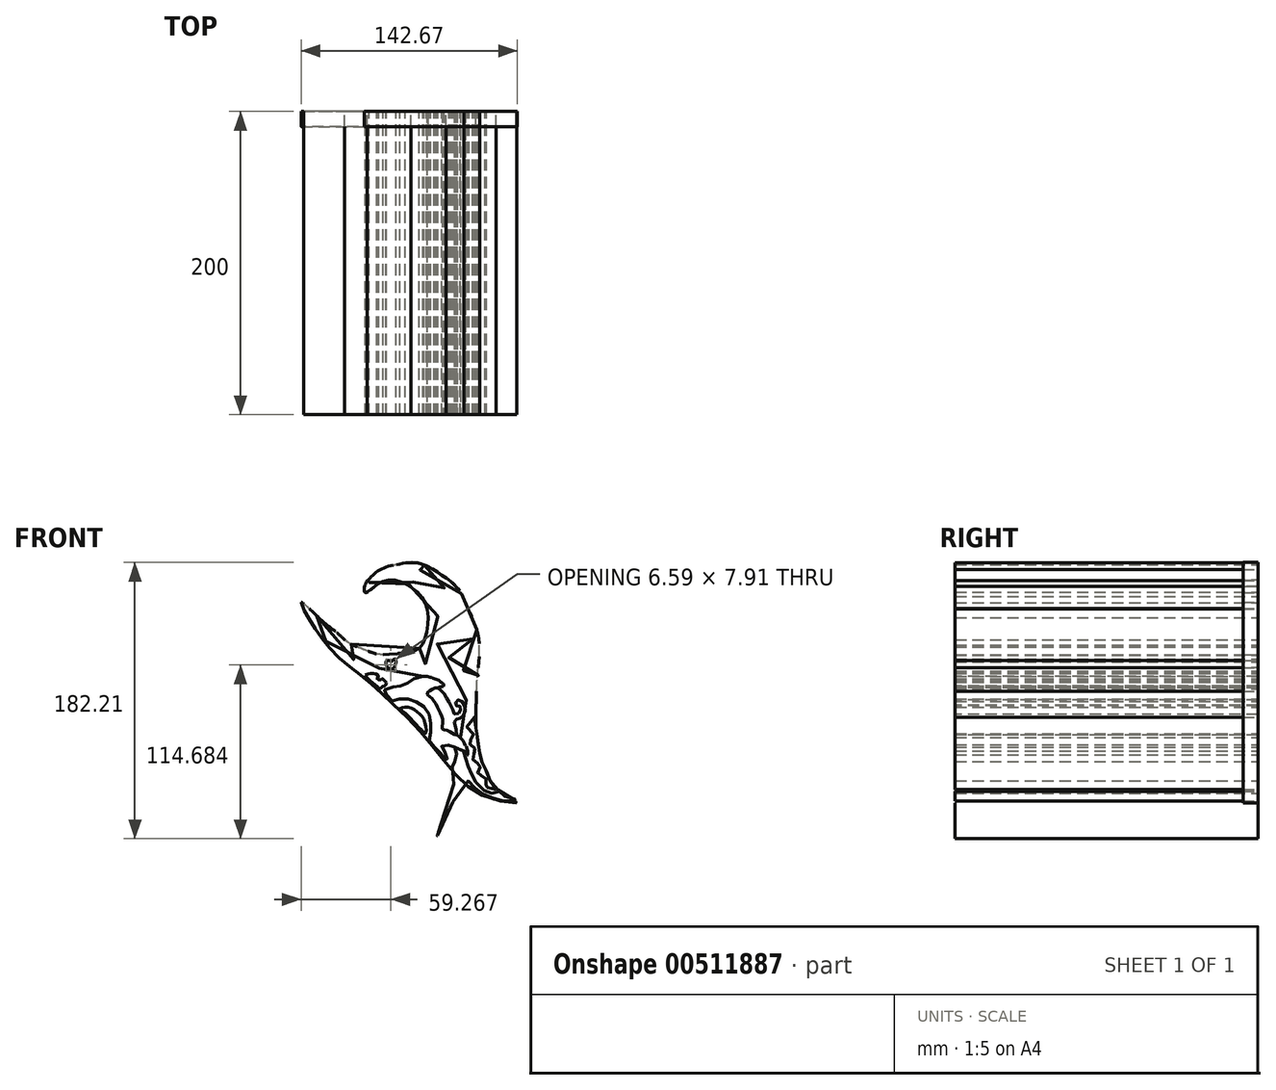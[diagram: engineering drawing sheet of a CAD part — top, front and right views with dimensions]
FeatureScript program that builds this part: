
annotation { "Feature Type Name" : "Feature", "Feature Type Description" : "" }
export const myFeature = defineFeature(function(context is Context, id is Id, definition is map)
    precondition{}
    {
        {
            var Q0;
            Q0=qCreatedBy(makeId("Front.planeOp"),FACE);
            var sketch = newSketch(context, id + "F0", { "sketchPlane" : qUnion([Q0])});
            skFitSpline(sketch, "E0", {"points": [v(-61.66, -100.95) * mm, v(-60.75, -105.22) * mm, v(-59.1, -108.17) * mm, v(-57.14, -111.12) * mm, v(-54.68, -114.57) * mm, v(-53.37, -117.36) * mm, v(-51.24, -119.98) * mm, v(-48.78, -124.4) * mm, v(-45.82, -127.69) * mm, v(-42.7, -130.8) * mm, v(-40.18, -133.76) * mm, v(-37.62, -136.55) * mm, v(-34.34, -139.83) * mm, v(-29.91, -143.1) * mm, v(-24.17, -146.39) * mm, v(-20.71, -144.2) * mm, v(-17.3, -143.74) * mm, v(-13.44, -143.59) * mm, v(-10.03, -145.44) * mm, v(-6.47, -148.54) * mm, v(-5.39, -151.48) * mm, v(-3.06, -153.34) * mm, v(-2.13, -150.7) * mm, v(0, -148.85) * mm, v(2.2, -147) * mm, v(4.83, -146.22) * mm, v(8.08, -146.06) * mm, v(11.64, -147) * mm, v(15.2, -148.08) * mm, v(16.9, -149.62) * mm, v(12.88, -150.4) * mm, v(9.48, -151.95) * mm, v(7.15, -153.5) * mm, v(4.52, -155.5) * mm, v(1.74, -155.82) * mm, v(0, -155.82) * mm, v(-3.53, -156.6) * mm, v(-7.09, -157.98) * mm, v(-9.41, -159.38) * mm, v(-7.45, -161.38) * mm, v(-4.91, -163.81) * mm, v(-2.96, -166.06) * mm, v(0, -164.89) * mm, v(2.8, -164.5) * mm, v(6.6, -164.5) * mm, v(10.6, -165.28) * mm, v(14, -167.03) * mm, v(17.42, -169.37) * mm, v(19.96, -172.5) * mm, v(21.61, -176.69) * mm, v(22.1, -180.5) * mm, v(22.2, -184.26) * mm, v(21.9, -188.03) * mm, v(20.92, -191.22) * mm, v(22.9, -193.83) * mm, v(25.33, -196.79) * mm, v(27.76, -199.17) * mm, v(29.97, -202.23) * mm, v(31.62, -204.43) * mm, v(33.96, -205.68) * mm, v(32.65, -203.33) * mm, v(31.69, -200.57) * mm, v(30.8, -198.23) * mm, v(30.03, -196.78) * mm, v(29.34, -195.6) * mm, v(31.69, -194.78) * mm, v(33.96, -194.85) * mm, v(35.83, -195.12) * mm, v(37.83, -196.02) * mm, v(39.27, -197.6) * mm, v(39.2, -200.85) * mm, v(38.52, -203.2) * mm, v(37.62, -206.23) * mm, v(36.8, -207.81) * mm, v(36.17, -208.99) * mm, v(38.25, -211.76) * mm, v(25.48, -256.62) * mm, v(45.7, -218.55) * mm, v(48.76, -221.5) * mm, v(51.83, -223.58) * mm, v(55.11, -226) * mm, v(58.86, -228.23) * mm, v(63.37, -229.89) * mm, v(68.06, -231.18) * mm, v(72.3, -231.64) * mm, v(75.98, -231.73) * mm, v(79.02, -231.09) * mm, v(73.95, -229.8) * mm, v(70.73, -228.32) * mm, v(68.98, -226.76) * mm, v(67.5, -225.47) * mm, v(65.58, -226.3) * mm, v(62.26, -226.58) * mm, v(59.5, -225.66) * mm, v(56.1, -224.27) * mm, v(52.1, -219.53) * mm, v(50.1, -215.8) * mm, v(48.36, -212.67) * mm, v(47.23, -209.98) * mm, v(46.19, -207.02) * mm, v(45.15, -203.9) * mm, v(44.28, -200.85) * mm, v(43.72, -198.81) * mm, v(45.3, -199.73) * mm, v(46.57, -201.35) * mm, v(46.46, -198.8) * mm, v(45.65, -196.14) * mm, v(44.49, -194.05) * mm, v(42.98, -191.26) * mm, v(41.47, -189.53) * mm, v(41.95, -187.01) * mm, v(42.47, -183.6) * mm, v(43.6, -180.3) * mm, v(44.85, -178.44) * mm, v(47.12, -176.68) * mm, v(49.8, -174.72) * mm, v(51.56, -174.1) * mm, v(51.77, -171.82) * mm, v(51.67, -170.27) * mm, v(51.54, -168.06) * mm, v(49.35, -167.04) * mm, v(47.15, -165.91) * mm, v(44.96, -164.7) * mm, v(42.18, -162.99) * mm, v(39.6, -160.94) * mm, v(33.4, -154.9) * mm, v(30.98, -151.8) * mm, v(29.33, -148.42) * mm, v(27.95, -144.76) * mm, v(26.85, -141.6) * mm, v(26.25, -136.27) * mm, v(26.18, -131.6) * mm, v(26.47, -126.85) * mm, v(27.28, -122.32) * mm, v(28.89, -118.3) * mm, v(31.37, -114.94) * mm, v(34.66, -112.23) * mm, v(37.29, -111.14) * mm, v(41.4, -110.8) * mm, v(45.4, -112.74) * mm, v(47.84, -116.25) * mm, v(49.5, -120.45) * mm, v(49.98, -126.4) * mm, v(49.5, -131.37) * mm, v(47.2, -135.46) * mm, v(45.02, -137.87) * mm, v(41.4, -138.74) * mm, v(38.12, -136.88) * mm, v(36.8, -134.04) * mm, v(36.7, -131.52) * mm, v(36.04, -129) * mm, v(34.84, -131.4) * mm, v(34.07, -134.36) * mm, v(34.07, -137.54) * mm, v(34.73, -141.04) * mm, v(36.37, -145.1) * mm, v(38.45, -148.05) * mm, v(41.3, -151.77) * mm, v(43.92, -154.29) * mm, v(46.11, -155.82) * mm, v(50.04, -158) * mm, v(52.48, -159.17) * mm, v(53.26, -154.78) * mm, v(53.55, -150.97) * mm, v(53.65, -147.37) * mm, v(53.94, -144.54) * mm, v(52.77, -143.66) * mm, v(51.4, -144.05) * mm, v(49.26, -144.63) * mm, v(47.4, -146.3) * mm, v(47.3, -147.27) * mm, v(48.38, -147.46) * mm, v(50.04, -148.44) * mm, v(50.33, -150.39) * mm, v(48.87, -152.14) * mm, v(46.43, -152.34) * mm, v(44.68, -150.97) * mm, v(43.6, -148.63) * mm, v(43.7, -145.51) * mm, v(44.58, -142.49) * mm, v(46.72, -140.34) * mm, v(49.26, -139.47) * mm, v(51.3, -139.17) * mm, v(53.45, -138.88) * mm, v(54.05, -136.97) * mm, v(54.44, -134.05) * mm, v(54.3, -131.57) * mm, v(54.24, -129.03) * mm, v(53.92, -126.23) * mm, v(53.53, -123.37) * mm, v(53, -120.83) * mm, v(52.55, -118.3) * mm, v(51.47, -115.11) * mm, v(49.91, -111.08) * mm, v(48.28, -108.02) * mm, v(46.98, -105.1) * mm, v(44.57, -105.03) * mm, v(41.9, -104.77) * mm, v(38.85, -104.05) * mm, v(38.72, -103.27) * mm, v(40.47, -102.16) * mm, v(42.1, -100.73) * mm, v(43.99, -98.52) * mm, v(43.18, -96.08) * mm, v(41.32, -93.6) * mm, v(39.67, -91.54) * mm, v(37.8, -90.09) * mm, v(34.92, -90.2) * mm, v(32.44, -90.2) * mm, v(29.65, -90.2) * mm, v(25.72, -89.37) * mm, v(21.59, -88.02) * mm, v(18.8, -86.27) * mm, v(16, -84.1) * mm, v(14.56, -82.34) * mm, v(14.46, -80.07) * mm, v(15.28, -79.14) * mm, v(17.45, -79.55) * mm, v(19.62, -80.79) * mm, v(22.31, -83.27) * mm, v(24.69, -85.03) * mm, v(28.2, -86.16) * mm, v(32.23, -85.44) * mm, v(31.5, -84.2) * mm, v(28.72, -82.24) * mm, v(26.13, -80.58) * mm, v(22.93, -78.62) * mm, v(19.93, -76.97) * mm, v(16.72, -75.77) * mm, v(14.05, -75.25) * mm, v(11.57, -74.99) * mm, v(9.23, -74.92) * mm, v(10.01, -77.72) * mm, v(11.12, -80) * mm, v(12.49, -82.28) * mm, v(14.11, -84.56) * mm, v(16.52, -86.05) * mm, v(19.52, -88.14) * mm, v(24.96, -90.17) * mm, v(30.3, -91.1) * mm, v(35.4, -91.85) * mm, v(36.88, -93.23) * mm, v(37.3, -95.1) * mm, v(36.54, -96.13) * mm, v(34.37, -96.85) * mm, v(31.47, -96.85) * mm, v(27.87, -96.16) * mm, v(24.28, -95.11) * mm, v(21.26, -93.72) * mm, v(17.2, -92.1) * mm, v(13.72, -89.9) * mm, v(9.43, -86.76) * mm, v(6.88, -84.68) * mm, v(3.63, -81.08) * mm, v(1.9, -77.95) * mm, v(0.85, -75.98) * mm, v(-1.7, -75.98) * mm, v(-5.53, -77.02) * mm, v(-8.43, -78.07) * mm, v(-11.56, -80.04) * mm, v(-14.46, -82.24) * mm, v(-16.9, -84.9) * mm, v(-18.63, -87.7) * mm, v(-19.8, -90.94) * mm, v(-19.56, -93.95) * mm, v(-19.1, -92.8) * mm, v(-17.82, -91.52) * mm, v(-16.2, -90.24) * mm, v(-14.11, -88.85) * mm, v(-12.02, -87.8) * mm, v(-8.66, -86.3) * mm, v(-5.3, -85.95) * mm, v(-1.82, -85.72) * mm, v(2.59, -86.65) * mm, v(7.7, -88.62) * mm, v(10.94, -91.17) * mm, v(16.04, -95.11) * mm, v(19.17, -99.4) * mm, v(20.57, -101.5) * mm, v(23.7, -102.77) * mm, v(27.3, -103.93) * mm, v(31.82, -104.62) * mm, v(34.6, -104.86) * mm, v(30.2, -106.94) * mm, v(27.52, -109.15) * mm, v(24.58, -111.43) * mm, v(24.3, -114.28) * mm, v(24.12, -117.23) * mm, v(23.47, -119.71) * mm, v(22.55, -122.2) * mm, v(21.36, -124.22) * mm, v(20.07, -125.88) * mm, v(20.9, -128.37) * mm, v(21.63, -130.76) * mm, v(22.1, -133.52) * mm, v(21.45, -136.65) * mm, v(19.88, -139.5) * mm, v(17.4, -141.9) * mm, v(13.44, -143.28) * mm, v(9.76, -143.28) * mm, v(7, -142.27) * mm, v(5.43, -140.24) * mm, v(5.25, -139.14) * mm, v(7.55, -138.4) * mm, v(10.95, -138.12) * mm, v(13.71, -137.2) * mm, v(16.3, -135.09) * mm, v(17.3, -132.97) * mm, v(17.3, -130.12) * mm, v(13.4, -132.03) * mm, v(8.3, -133.9) * mm, v(3.8, -134.66) * mm, v(-2.23, -135.28) * mm, v(-7.5, -135.28) * mm, v(-12.3, -134.82) * mm, v(-17.1, -133.9) * mm, v(-22.51, -131.26) * mm, v(-26.7, -130.02) * mm, v(-30.72, -128) * mm, v(-34.43, -125.53) * mm, v(-33.98, -129.25) * mm, v(-31.4, -132.94) * mm, v(-28.09, -134.78) * mm, v(-24.15, -135.52) * mm, v(-21.57, -135.27) * mm, v(-19.12, -136.5) * mm, v(-18.87, -138.46) * mm, v(-20.71, -139.7) * mm, v(-24.15, -139.45) * mm, v(-27.96, -138.83) * mm, v(-30.91, -137.48) * mm, v(-33.5, -136.13) * mm, v(-35.21, -133.8) * mm, v(-36.56, -131.1) * mm, v(-37.67, -127.65) * mm, v(-38.9, -123.84) * mm, v(-39.39, -121.14) * mm, v(-42.06, -119.07) * mm, v(-45.87, -116.34) * mm, v(-49.38, -113.51) * mm, v(-52.7, -110.2) * mm, v(-56.79, -106.4) * mm, v(-59.13, -103.37) * mm, v(-61.66, -100.95) * mm]});
            skFitSpline(sketch, "E1", {"points": [v(-3.96, -139.84) * mm, v(-2.98, -138.86) * mm, v(-1.37, -138) * mm, v(-0.87, -139.25) * mm, v(-0.96, -141.26) * mm, v(-1.64, -143.06) * mm, v(-2.6, -144.18) * mm, v(-3.36, -145.15) * mm, v(-4.1, -145.9) * mm, v(-5.08, -145) * mm, v(-6.13, -143.8) * mm, v(-7.03, -142.6) * mm, v(-7.48, -141.26) * mm, v(-7.48, -139.99) * mm, v(-6.95, -139.16) * mm, v(-5.9, -138.94) * mm, v(-4.7, -139.31) * mm, v(-3.96, -139.84) * mm]});
            skFitSpline(sketch, "E2", {"points": [v(-20.97, -148.41) * mm, v(-18.71, -151.52) * mm, v(-16.6, -153.36) * mm, v(-14.47, -155.2) * mm, v(-12.63, -156.75) * mm, v(-11.79, -157.74) * mm, v(-10.66, -156.9) * mm, v(-9.38, -156.04) * mm, v(-8.11, -155.62) * mm, v(-7.26, -154.77) * mm, v(-7.26, -153.5) * mm, v(-8.54, -152.37) * mm, v(-9.95, -150.95) * mm, v(-10.66, -151.52) * mm, v(-12.07, -151.8) * mm, v(-13.34, -150.95) * mm, v(-13.06, -150.25) * mm, v(-12.07, -149.54) * mm, v(-13.48, -148.27) * mm, v(-15.18, -147.56) * mm, v(-17.3, -147.56) * mm, v(-19.14, -147.84) * mm, v(-20.97, -148.41) * mm]});
            skFitSpline(sketch, "E3", {"points": [v(19.68, -160.97) * mm, v(21.63, -163.07) * mm, v(24.48, -165.92) * mm, v(26.57, -169.51) * mm, v(28.07, -173.25) * mm, v(29.72, -177.15) * mm, v(29.87, -181.5) * mm, v(29.72, -184.04) * mm, v(31.67, -184.79) * mm, v(34.8, -185.98) * mm, v(37.5, -187.48) * mm, v(39.15, -188.08) * mm, v(39.15, -185.53) * mm, v(38.4, -182.39) * mm, v(37.95, -180.74) * mm, v(37.8, -178.8) * mm, v(39.15, -177.75) * mm, v(40.65, -177.3) * mm, v(42.9, -176.1) * mm, v(44.7, -173.4) * mm, v(44.7, -169.66) * mm, v(43.5, -166.82) * mm, v(41.4, -165.02) * mm, v(39.45, -165.32) * mm, v(38.4, -167.26) * mm, v(38.85, -168.91) * mm, v(40.8, -168.61) * mm, v(41.7, -170.26) * mm, v(41.7, -172.2) * mm, v(40.5, -174) * mm, v(38.1, -174.6) * mm, v(36.76, -172.2) * mm, v(36, -169.81) * mm, v(34.8, -167.71) * mm, v(33.61, -165.32) * mm, v(32.11, -162.77) * mm, v(30.47, -160.38) * mm, v(28.97, -158.88) * mm, v(26.87, -157.08) * mm, v(23.43, -157.83) * mm, v(21.18, -159.18) * mm, v(19.68, -160.97) * mm]});
            skFitSpline(sketch, "E4", {"points": [v(65.23, -224) * mm, v(61.84, -219.36) * mm, v(59.17, -212.41) * mm, v(56.5, -207.25) * mm, v(54.72, -201.73) * mm, v(54, -196.74) * mm, v(52.58, -189.98) * mm, v(52.23, -184.45) * mm, v(51.51, -179.47) * mm, v(50.98, -176.44) * mm, v(46, -183.39) * mm, v(50.27, -187.66) * mm, v(49.2, -189.8) * mm, v(48.13, -192.11) * mm, v(47.42, -193.54) * mm, v(48.84, -195.14) * mm, v(50.45, -196.92) * mm, v(52.4, -197.99) * mm, v(50.27, -201.02) * mm, v(49.56, -202.98) * mm, v(50.45, -204.94) * mm, v(51.87, -205.83) * mm, v(53.83, -207.43) * mm, v(54.9, -208.5) * mm, v(53.83, -210.81) * mm, v(53.3, -212.77) * mm, v(52.76, -214.02) * mm, v(55.08, -214.9) * mm, v(57.21, -215.98) * mm, v(58.82, -217.22) * mm, v(58.82, -219.54) * mm, v(58.28, -221.32) * mm, v(57.93, -222.39) * mm, v(60.95, -223.28) * mm, v(65.23, -224) * mm]});
            skFitSpline(sketch, "E5", {"points": [v(1.82, -170.7) * mm, v(4.5, -173.23) * mm, v(7.7, -176.03) * mm, v(10.1, -178.84) * mm, v(13.31, -182.18) * mm, v(15.85, -184.79) * mm, v(17.85, -187.4) * mm, v(19.2, -185.98) * mm, v(18.92, -182.58) * mm, v(17.85, -178.57) * mm, v(16.25, -175.63) * mm, v(14.11, -173.63) * mm, v(11.44, -171.63) * mm, v(8.23, -170.16) * mm, v(5.43, -169.76) * mm, v(3.42, -170.02) * mm, v(1.82, -170.7) * mm]});
            skFitSpline(sketch, "E6", {"points": [v(16.9, -149.62) * mm, v(20.15, -149.62) * mm, v(23.37, -150.53) * mm, v(26.82, -151.84) * mm, v(28.96, -153.39) * mm, v(30.63, -154.94) * mm, v(30.03, -156.13) * mm, v(28.13, -156.48) * mm, v(26.87, -157.08) * mm], "startDerivative": vector(22.67, 1.55) * mm, "endDerivative": vector(-11.85, -7.74) * mm});
            skFitSpline(sketch, "E7", {"points": [v(39.12, -187.94) * mm, v(41.9, -190.12) * mm], "startDerivative": vector(2.68, -2) * mm, "endDerivative": vector(2.68, -2) * mm});
            skFitSpline(sketch, "E8", {"points": [v(37.83, -196.02) * mm, v(39.36, -196.81) * mm, v(40.57, -197.35) * mm, v(41.83, -197.97) * mm, v(42.74, -198.26) * mm, v(43.72, -198.81) * mm], "startDerivative": vector(6.85, -3.73) * mm, "endDerivative": vector(5.3, -3.4) * mm});
            skSolve(sketch);
        }
        {
            var Q0;
            Q0=makeQuery(id+"F0.imprint","IMPRINT",FACE,{"disambiguationData":[TD([[makeQuery(id+"F0.imprint","IMPRINT",EDGE,{"derivedFrom":sQuery(id+"F0.wireOp",EDGE,"E4")}),1.0]])]});
            var Q1;
            Q1=makeQuery(id+"F0.imprint","IMPRINT",FACE,{"disambiguationData":[TD([[makeQuery(id+"F0.imprint","IMPRINT",EDGE,{"derivedFrom":sQuery(id+"F0.wireOp",EDGE,"E1")}),1.0]])]});
            var Q2;
            {var subQ0=sQuery(id+"F0.wireOp",EDGE,"E8");Q2=makeQuery(id+"F0.imprint","IMPRINT",FACE,{"disambiguationData":[TD([[makeQuery(id+"F0.imprint","IMPRINT",EDGE,{"derivedFrom":subQ0}),-1.0]])]});}
            extrude(context, id + "F1", {"entities" : qUnion([Q0, Q1, Q2]), "depth" : 200 * mm});
        }
        {
            var Q0;
            {var subQ0=sQuery(id+"F0.wireOp",EDGE,"E6");Q0=makeQuery(id+"F0.imprint","IMPRINT",FACE,{"disambiguationData":[TD([[makeQuery(id+"F0.imprint","IMPRINT",EDGE,{"derivedFrom":subQ0}),-1.0]])]});}
            var Q1;
            Q1=makeQuery(id+"F0.imprint","IMPRINT",FACE,{"disambiguationData":[TD([[makeQuery(id+"F0.imprint","IMPRINT",EDGE,{"derivedFrom":sQuery(id+"F0.wireOp",EDGE,"E2")}),1.0]])]});
            var Q2;
            Q2=makeQuery(id+"F0.imprint","IMPRINT",FACE,{"disambiguationData":[TD([[makeQuery(id+"F0.imprint","IMPRINT",EDGE,{"derivedFrom":sQuery(id+"F0.wireOp",EDGE,"E5")}),1.0]])]});
            extrude(context, id + "F2", {"entities" : qUnion([Q0, Q1, Q2]), "depth" : 200 * mm});
        }
        {
            var Q0;
            Q0=qCreatedBy(makeId("Front.planeOp"),FACE);
            var sketch = newSketch(context, id + "F3", { "sketchPlane" : qUnion([Q0])});
            skFitSpline(sketch, "E9", {"points": [v(-63.32, -100.76) * mm, v(-61.91, -105.1) * mm, v(-58.33, -111.1) * mm, v(-53.12, -119.47) * mm, v(-47.3, -127.58) * mm, v(-37.93, -137.8) * mm, v(-27.92, -145.67) * mm, v(-16.78, -154.78) * mm, v(-5.91, -164.94) * mm, v(12.98, -183.08) * mm, v(28.35, -202.08) * mm, v(44.7, -220.22) * mm, v(62.5, -230.5) * mm, v(79.17, -232.57) * mm, v(69.6, -226.61) * mm, v(60.67, -217.28) * mm, v(54.37, -200.67) * mm, v(52.1, -184.24) * mm, v(52.08, -168.22) * mm, v(52.99, -148.43) * mm, v(54.29, -131.5) * mm, v(51.9, -116.48) * mm, v(46.21, -103.46) * mm, v(39.14, -90.64) * mm, v(26.84, -81.02) * mm, v(13.59, -74.71) * mm, v(0, -75.69) * mm, v(-10.62, -78.76) * mm, v(-17.63, -84.33) * mm, v(-21.22, -89.07) * mm, v(-21.25, -94.03) * mm, v(-15.33, -90.74) * mm, v(-9.17, -86.7) * mm, v(0, -86.39) * mm, v(7.91, -90) * mm, v(15.91, -96.68) * mm, v(20.03, -106.02) * mm, v(19.68, -118.8) * mm, v(17, -127.66) * mm, v(11.98, -132.25) * mm, v(-3.6, -134.75) * mm, v(-12.42, -134.91) * mm, v(-22.42, -131.7) * mm, v(-33, -126.79) * mm, v(-39.47, -120.96) * mm, v(-48.6, -113.73) * mm, v(-63.32, -100.76) * mm]});
            skSolve(sketch);
        }
        {
            var Q0;
            Q0 = qSketchRegion(id + "F3", true);
            extrude(context, id + "F4", {"entities" : qUnion([Q0]), "depth" : 10 * mm, "offsetDistance" : 25 * mm});
        }
    });
